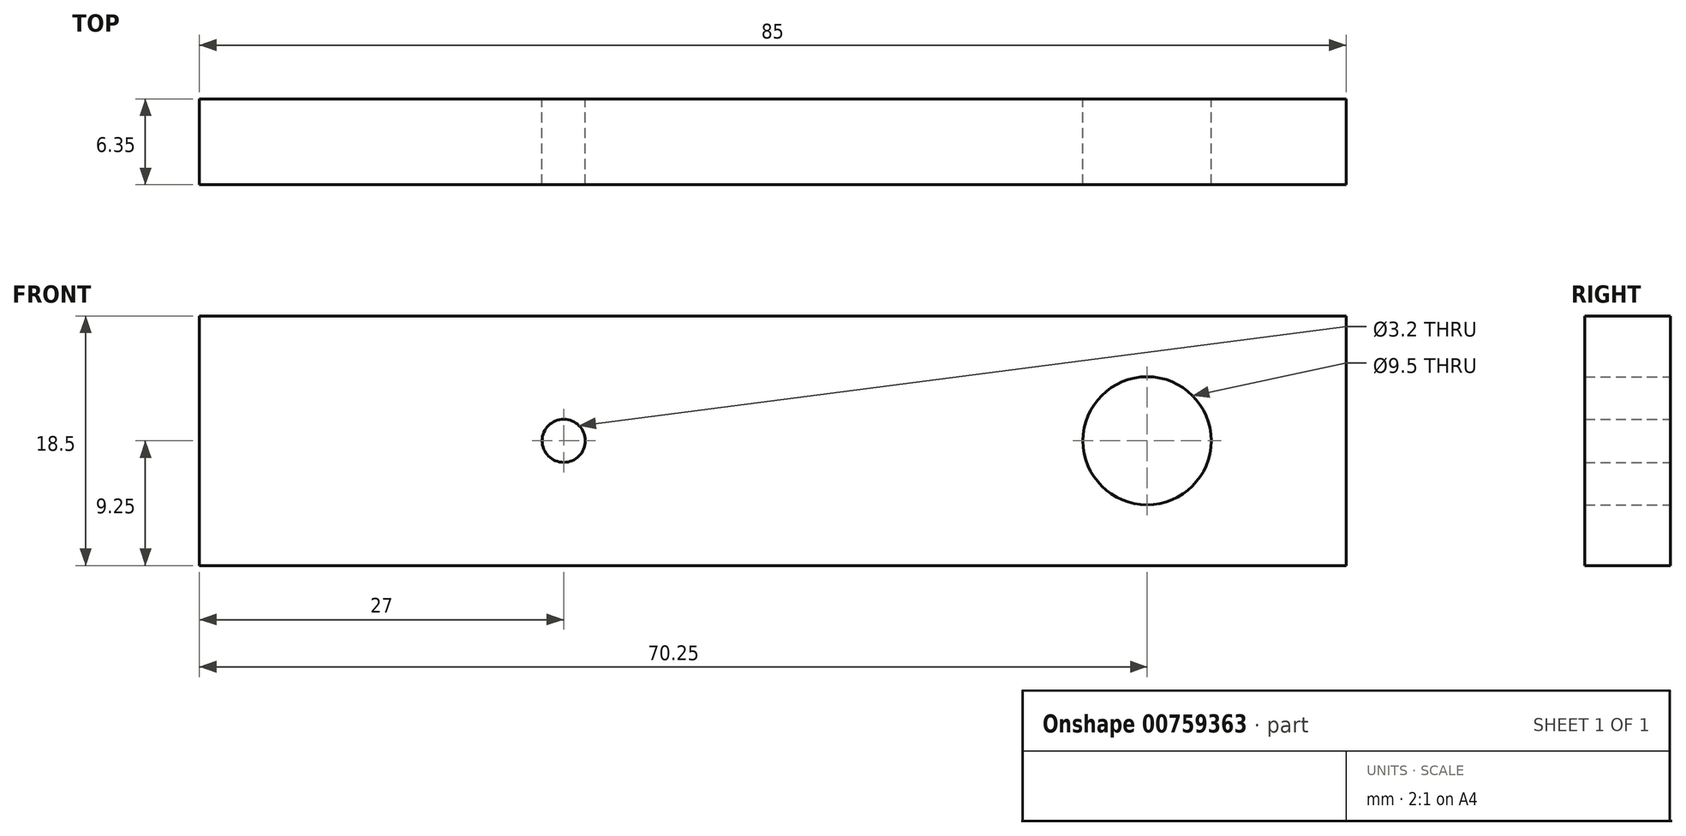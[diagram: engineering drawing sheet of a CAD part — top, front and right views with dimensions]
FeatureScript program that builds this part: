
annotation { "Feature Type Name" : "Feature", "Feature Type Description" : "" }
export const myFeature = defineFeature(function(context is Context, id is Id, definition is map)
    precondition{}
    {
        {
            var Q0;
            Q0=qCreatedBy(makeId("Front.planeOp"),FACE);
            var sketch = newSketch(context, id + "F0", { "sketchPlane" : qUnion([Q0])});
            skLineSegment(sketch, "E0.bottom", {"start": v(42.5, 9.25) * mm, "end": v(-42.5, 9.25) * mm});
            skLineSegment(sketch, "E0.top", {"start": v(42.5, -9.25) * mm, "end": v(-42.5, -9.25) * mm});
            skLineSegment(sketch, "E0.left", {"start": v(42.5, 9.25) * mm, "end": v(42.5, -9.25) * mm});
            skLineSegment(sketch, "E0.right", {"start": v(-42.5, 9.25) * mm, "end": v(-42.5, -9.25) * mm});
            skPoint(sketch, "E0.middle", {"position": v(0, 0) * mm});
            skCircle(sketch, "E1", {"center": v(-15.5, 0) * mm, "radius": 1.6 * mm});
            skCircle(sketch, "E2", {"center": v(27.75, 0) * mm, "radius": 4.75 * mm});
            skSolve(sketch);
        }
        {
            var Q0;
            Q0=makeQuery(id+"F0.imprint","IMPRINT",FACE,{"disambiguationData":[TD([[makeQuery(id+"F0.imprint","IMPRINT",EDGE,{"derivedFrom":sQuery(id+"F0.wireOp",EDGE,"E0.bottom")}),1.0]])]});
            extrude(context, id + "F1", {"entities" : qUnion([Q0]), "depth" : 6.35 * mm, "offsetDistance" : 25 * mm});
        }
    });
